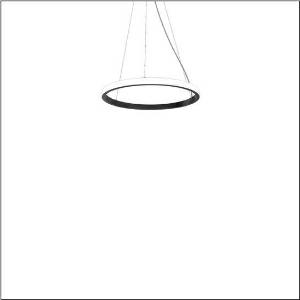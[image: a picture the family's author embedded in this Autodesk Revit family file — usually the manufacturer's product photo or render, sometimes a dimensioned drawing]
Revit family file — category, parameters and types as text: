
# Revit family: silica_21_ring-o_5pjbo1d1104a
name_source: partatom
category: Lighting Fixtures
units: mm (PartAtom-declared; Revit-internal decimal feet)

## family parameters
Cut with Voids When Loaded = No
Host = Face
Light Source = No
Part Type = Normal
Room Calculation Point = No
Round Connector Dimension = Use Diameter
Shared = No

## types (1)
- Silica 21 Ring-O (1 x LED, 3740 lm, 60 W, 3000K)
    Apparent Load = 60 VA
    CIE Flux Codes = 2 16 49 50 100
    Color Rendering = 80
    Color Temperature = 3000K
    Default Elevation = 1800 mm
    Description = Silica 21 Ring-O, suspended luminaire, of PMMA, frosted, light emission: outer ring side luminous distribution, primary light characteristic: symmetric, installation type: suspended mounting, LED, rated luminous flux: 3.744lm, luminous efficacy: 62lm/W, light colour: 830, colour temperature: 3000K, control gear: DALI 2, with terminal, 5-pole, mains connection: 230V, AC/DC, 0/50..60Hz, rated input power: 60W, housing, of extruded aluminium section, jet black (RAL 9005), diameter: 610mm, ceiling canopy, jet black (RAL 9005), protection rating (lamp compartment): IP40, insulation class (complete): insulation class I (protective earthing), certification: CE, impact resistance: IK02, permissible operating ambient temperature: 0..+35°C, packaging unit: 1 piece
    Height = 48 mm  [stored 0.15748 ft]
    Lamp = 1 x LED
    Lamp Light Flux = 3740 lm
    Lamp Power = 60 W
    Lamp count = 1
    Length = 610 mm
    Luminous efficacy = 62 lm/W
    Manufacturer = Siteco
    ModVariant = No
    Model = 5PJBO1D1104A
    Mounting Place = Ceiling
    Mounting Type = Pendant
    Number of Poles = 1
    OnlyDefault = Yes
    Power Factor = 1
    Product Name = Silica 21 Ring-O
    Product group = suspended luminaire
    ProductGroupID = 904
    Protection Class = Protection class I
    Protection Degree = IP 40
    RLX_Detail_Level = 1
    RLX_Emergency_Light_Flux = 0 lm
    RLX_Emergency_Type = 0
    RLX_Emergency_Type_DB = No
    RlxData = <blob elided: 12141 chars, md5=340696c3>
    Socket = socket
    Standby Power = 0 W
    System Light Flux = 3740 lm
    System Power = 60 W
    Type Comments = Product without accessories
    Type Image = l_1258377.jpg
    URL = http://relux.com
    VarID = ---
    Voltage = 0 V
    Weight = 0.00 kg
    Width = 0 mm  [stored 0 ft]

note: [stored X ft] marks values corroborated as IEEE doubles in the binary element streams (Revit-internal decimal feet)

## geometry (parser evidence)
native form markers: Sweep x12
no freeform markers — native parametric forms only
